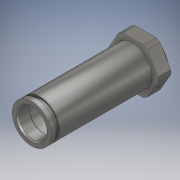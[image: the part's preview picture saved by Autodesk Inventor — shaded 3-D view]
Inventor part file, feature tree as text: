
AUTODESK INVENTOR PART (.ipt)
format: ipt  version: 2019 (Build 230136000, 136)  size: 221,184 bytes
history: native  units: mm
features: chamfer x3, sketch x3, other x2, extrude x1, hole x1, pattern_circular x1, projected_geometry x1
ambient origin geometry x8: Origin, YZ Plane, XZ Plane, XY Plane, X Axis, Y Axis, Z Axis, Center Point
bodies: Solide1 (feature_tree)
feature tree (12):
  other  "Révolution1"
  other  "Plan de construction1"
  extrude  "Extrusion1"  Depth=30.0mm
  chamfer  "Chanfrein1"  Distance=8.0mm
  chamfer  "Chanfrein2"  Distance=4.0mm
  hole  "Perçage1"  [1 undecoded]
  chamfer  "Chanfrein3"  Distance=2.0mm
  pattern_circular  "Réseau circulaire1"  [2 undecoded]
  sketch  "Esquisse1"
  sketch  "Esquisse3"
  sketch  "Esquisse4"
  projected_geometry  "Boucle projetée1"
note: 3 required parameter values undecoded (feature->parameter linkage not recoverable at this tier; creation-order binding heuristic only, values carry confidence <= 0.55)
